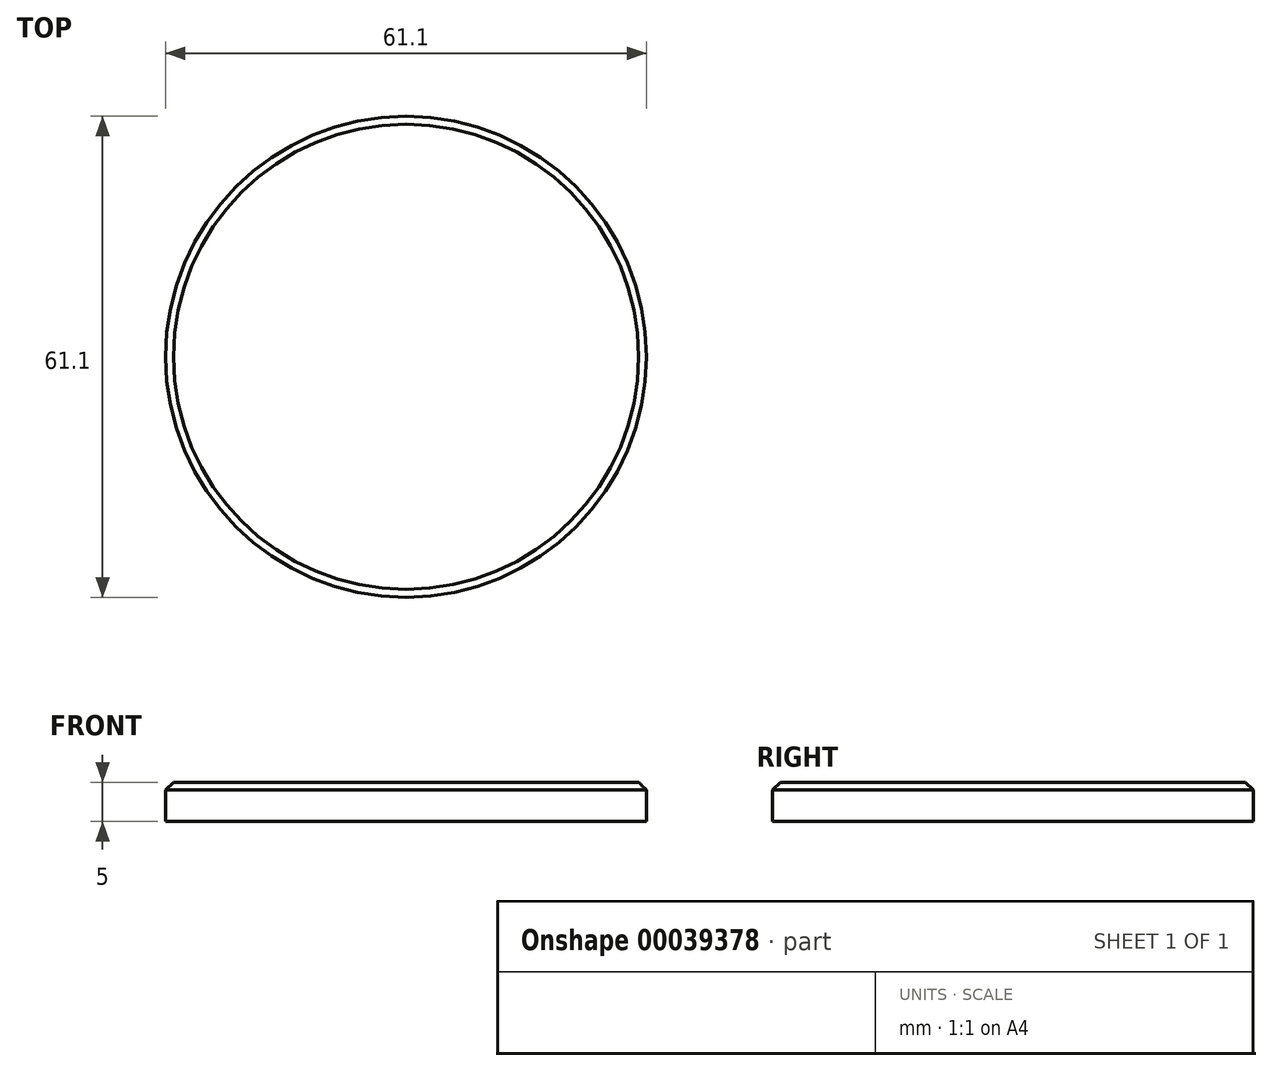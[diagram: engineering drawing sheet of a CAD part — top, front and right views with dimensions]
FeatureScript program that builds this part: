
annotation { "Feature Type Name" : "Feature", "Feature Type Description" : "" }
export const myFeature = defineFeature(function(context is Context, id is Id, definition is map)
    precondition{}
    {
        {
            var Q0;
            Q0=qCreatedBy(makeId("Top.planeOp"),FACE);
            var sketch = newSketch(context, id + "F0", { "sketchPlane" : qUnion([Q0])});
            skCircle(sketch, "E0", {"center": v(0, 0) * mm, "radius": 30.55 * mm});
            skSolve(sketch);
        }
        {
            var Q0;
            Q0=makeQuery(id+"F0.imprint","IMPRINT",FACE,{"disambiguationData":[TD([[makeQuery(id+"F0.imprint","IMPRINT",EDGE,{"derivedFrom":sQuery(id+"F0.wireOp",EDGE,"E0")}),1.0]])]});
            extrude(context, id + "F1", {"entities" : qUnion([Q0]), "depth" : 5 * mm});
        }
        {
            var Q0;
            Q0=makeQuery(id+"F1.opExtrude","CAP_EDGE",EDGE,{"disambiguationData":[OSD([sQuery(id+"F0.wireOp",EDGE,"E0")])],"isStart":false});
            chamfer(context, id + "F2", {"entities" : qUnion([Q0]), "width" : 1 * mm, "tangentPropagation" : true});
        }
        {
            var Q0;
            Q0=makeQuery(id+"F1.opExtrude","CAP_FACE",FACE,{"disambiguationData":[OSD([sQuery(id+"F0.wireOp",EDGE,"E0")])],"isStart":false});
            var sketch = newSketch(context, id + "F3", { "sketchPlane" : qUnion([Q0])});
            skCircle(sketch, "E1", {"center": v(9.27, 0) * mm, "radius": 4.46 * mm});
            skCircle(sketch, "E2", {"center": v(-9.84, 0) * mm, "radius": 4.47 * mm});
            skSolve(sketch);
        }
        {
            var Q0;
            Q0=sQuery(id+"F3.wireOp",EDGE,"E2");
            var Q1;
            Q1=sQuery(id+"F3.wireOp",EDGE,"E1");
            extrude(context, id + "F4", {"bodyType" : ToolBodyType.SURFACE, "surfaceEntities" : qUnion([Q0, Q1]), "depth" : 25 * mm});
        }
    });
